# Revit family: Faucet_Single_Control-American_Standard-Pekoe-4332.350
name_source: partatom
category: Plumbing Fixtures
revit_build: Autodesk Revit 2018 (Build: 20170223_1515(x64)
units: mm (PartAtom-declared; Revit-internal decimal feet)

## family parameters
Always vertical = No
Cut with Voids When Loaded = No
OmniClass Number = 23.45.55.14
OmniClass Title = Single Faucets
Part Type = Normal
Room Calculation Point = No
Round Connector Dimension = Use Radius
Shared = Yes
Work Plane-Based = Yes

## types (2) — shared parameters
ADA Compliant = Yes
Assembly Code = D2020300
CW Connection = Yes
CWFU = 1.5
Cold Water Connection Diameter = 1/2"
Cold Water Connection Radius = 0"
Default Elevation = 0"
Description = Pekoe Single Control Kitchen Faucet Semi-Professional.
Flow Rate = 1.5 gpm (5.7 Lpm)
HW Connection = Yes
HWFU = 1.5
Height = 21 1/2"
Hot Water Connection Diameter = 1/2"
Hot Water Connection Radius = 0"
IAPMO Compliance = Product meets or exceeds: ANSI A117.1, ASME A112.18.1, NSF 61/Section 9 & Annex G, CSA B125.1
Installation Type = Deck Mounted
Length = 8 1/2"
Manufacturer = American Standard
Product Documentation Link = https://www.americanstandard-us.com
Product Page URL = https://www.americanstandard-us.com
Revised Date = 04/20/2021
URL = http://www.americanstandard.com
Vent Connection = No
Warranty Information = Lifetime warranty
Waste Connection = No
Width = 1 1/2"
zero-valued in all types: WFU

## per-type parameters (varying)
| type | Body Material |
| 4332.350.002 | Metal-American_Standard-002-Polished_Chrome |
| 4332.350.075 | Metal-American_Standard-075-Stainless_Steel |

note: column(s) folded — value = type name in every type: Model

## geometry (parser evidence)
native form markers: Sweep x2
no freeform markers — native parametric forms only
